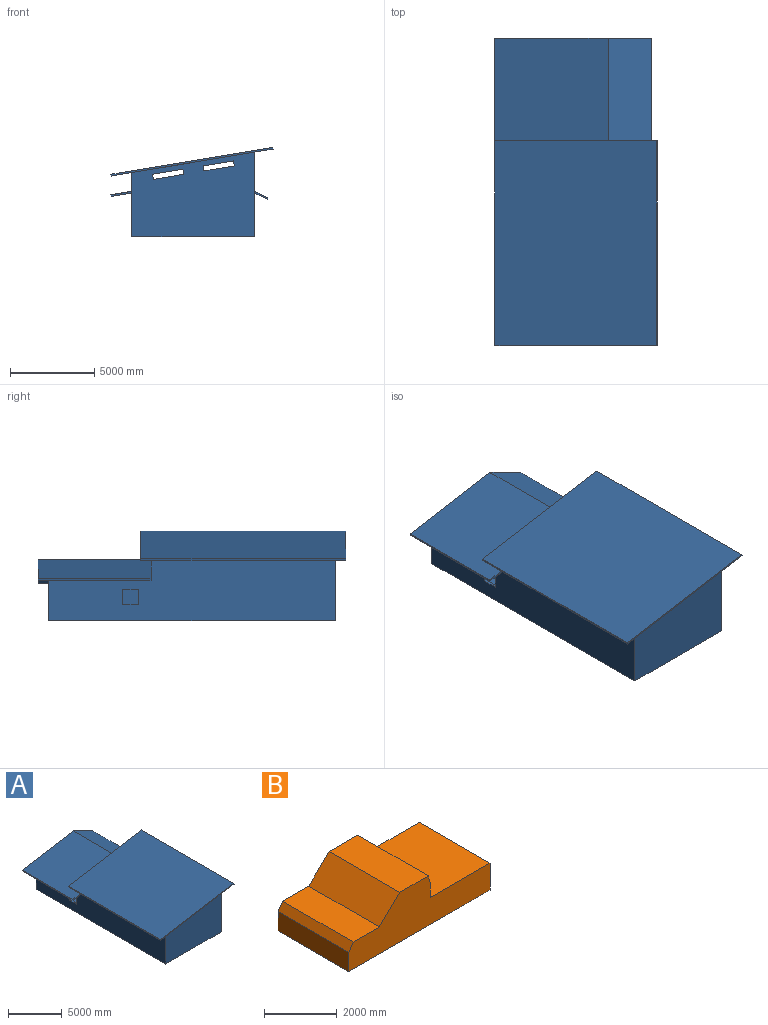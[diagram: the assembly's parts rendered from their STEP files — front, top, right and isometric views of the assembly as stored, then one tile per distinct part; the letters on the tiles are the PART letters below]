
ASSEMBLY  parts=2 mates=1
PART A: 106 faces, bbox 9637.6x18288x5310.4 mm
  f0: plane 7162.8x6096mm, normal (0,0,1), area 41367720.6mm2, adj f1,f2,f3,f6,f13,f15,f16,f41
  f1: plane 5181.6x3172.9mm, normal (0,1,0), area 13971038.2mm2, adj f0,f2,f3,f5,f88,f90,f91
  f2: plane 5943.6x2309.3mm, normal (1,0,0), area 12657180.9mm2, adj f0,f1,f5,f41,f56,f57,f58,f59
  f3: plane 5943.6x3172.9mm, normal (-1,0,0), area 15328305.8mm2, adj f0,f1,f5,f41,f49,f50,f51,f52
  f4: plane 10668x7162.8mm, normal (0,0,1), area 75715977.6mm2, adj f9,f10,f12,f13,f14,f44,f45,f47
  f5: plane 5943.6x5181.6mm, normal (0.16,0,-0.99), area 31222169mm2, adj f1,f2,f3,f41
  f6: plane 6096x3352.8mm, normal (1,0,0), area 16908539.1mm2, adj f0,f15,f16,f29,f49,f50,f51,f52
  f7: plane 7315.2x2335.5mm, normal (0,1,0), area 8165969.2mm2, adj f11,f13,f19,f26,f27,f60,f61,f62
  f8: plane 7315.2x5029.2mm, normal (0,-1,0), area 31215421.4mm2, adj f11,f13,f17,f19,f68,f69,f70,f71
  f9: plane 7010.4x4799.8mm, normal (0,1,0), area 28438179.7mm2, adj f4,f12,f14,f42,f68,f69,f70,f71
  f10: plane 7010.4x4799.8mm, normal (0,-1,0), area 28438179.7mm2, adj f4,f12,f14,f42,f60,f61,f62,f63
  f11: plane 17068.8x3810mm, normal (-1,0,0), area 56763757.4mm2, adj f7,f8,f15,f17,f19,f24,f32,f56
  f12: plane 10668x3631.4mm, normal (1,0,0), area 38739735.5mm2, adj f4,f9,f10,f42
  f13: plane 17068.8x5029.2mm, normal (1,0,0), area 33816706.6mm2, adj f0,f4,f7,f8,f15,f16,f17,f19
  f14: plane 10668x4799.8mm, normal (-1,0,0), area 28907497.1mm2, adj f4,f9,f10,f42,f43,f44,f45,f46
  f15: plane 7315.2x3505.2mm, normal (0,1,0), area 15329001.6mm2, adj f0,f6,f11,f13,f17,f24,f33,f34
  f16: plane 3352.8x1828.8mm, normal (0,1,0), area 5295473.3mm2, adj f0,f6,f13,f29
  f17: plane 17068.8x7315.2mm, normal (0,0,-1), area 124861685.8mm2, adj f8,f11,f13,f15
  f18: plane 12192x100.12mm, normal (-0.99,0,-0.16), area 1237468.5mm2, adj f19,f21,f22,f23
  f19: plane 12192x9620.89mm, normal (0.16,0,-0.99), area 37540464.4mm2, adj f7,f8,f11,f13,f18,f20,f21,f22
  f20: plane 12192x100.12mm, normal (0.99,0,0.16), area 1237468.5mm2, adj f19,f21,f22,f23
  f21: plane 9637.58x1703.6mm, normal (0,-1,0), area 989974.8mm2, adj f18,f19,f20,f23
  f22: plane 9637.58x1703.6mm, normal (0,1,0), area 989974.8mm2, adj f18,f19,f20,f23
  f23: plane 12192x9620.89mm, normal (-0.16,0,0.99), area 118915891.2mm2, adj f18,f20,f21,f22
  f24: plane 6705.6x6705.6mm, normal (0.16,0,-0.99), area 11678880.7mm2, adj f11,f15,f28,f29,f31,f32
  f25: plane 762x483.9mm, normal (0,-1,0), area 78408.6mm2, adj f13,f26,f29,f30
  f26: plane 6705.6x2590.8mm, normal (0.45,0,0.89), area 19423457.4mm2, adj f7,f25,f27,f30,f31
  f27: plane 6722.29x6705.6mm, normal (-0.16,0,0.99), area 45698743.2mm2, adj f7,f26,f28,f31,f32
  f28: plane 6705.6x100.12mm, normal (-0.99,0,-0.16), area 680607.7mm2, adj f24,f27,f31,f32
  f29: plane 6705.6x2590.8mm, normal (-0.45,0,-0.89), area 19423457.4mm2, adj f6,f16,f24,f25,f30,f31
  f30: plane 6705.6x102.9mm, normal (1,0,0), area 689995.8mm2, adj f25,f26,f29,f31
  f31: plane 9313.09x1398.3mm, normal (0,1,0), area 957443.6mm2, adj f24,f26,f27,f28,f29,f30
  f32: plane 1235.89x306.1mm, normal (0,-1,0), area 126312.3mm2, adj f11,f24,f27,f28
  f33: plane 914.4x152.4mm, normal (0,0,-1), area 139354.6mm2, adj f15,f34,f36,f41
  f34: plane 914.4x152.4mm, normal (1,0,0), area 139354.6mm2, adj f15,f33,f35,f41
  f35: plane 914.4x152.4mm, normal (0,0,1), area 139354.6mm2, adj f15,f34,f36,f41
  f36: plane 914.4x152.4mm, normal (-1,0,0), area 139354.6mm2, adj f15,f33,f35,f41
  f37: plane 914.4x152.4mm, normal (-1,0,0), area 139354.6mm2, adj f15,f38,f40,f41
  f38: plane 914.4x152.4mm, normal (0,0,-1), area 139354.6mm2, adj f15,f37,f39,f41
  f39: plane 914.4x152.4mm, normal (1,0,0), area 139354.6mm2, adj f15,f38,f40,f41
  f40: plane 914.4x152.4mm, normal (0,0,1), area 139354.6mm2, adj f15,f37,f39,f41
  f41: plane 5181.6x3172.9mm, normal (0,-1,0), area 12298783.4mm2, adj f0,f2,f3,f5,f33,f34,f35,f36
  f42: plane 10668x7010.4mm, normal (0.16,0,-0.99), area 75818540mm2, adj f9,f10,f12,f14
  f43: plane 3657.6x152.4mm, normal (0,0,-1), area 557418.2mm2, adj f13,f14,f44,f45
  f44: plane 3657.6x152.4mm, normal (0,1,0), area 557418.2mm2, adj f4,f13,f14,f43
  f45: plane 3657.6x152.4mm, normal (0,-1,0), area 557418.2mm2, adj f4,f13,f14,f43
  f46: plane 3657.6x152.4mm, normal (0,0,-1), area 557418.2mm2, adj f13,f14,f47,f48
  f47: plane 2438.4x152.4mm, normal (0,1,0), area 371612.2mm2, adj f4,f13,f14,f46
  f48: plane 2438.4x152.4mm, normal (0,-1,0), area 371612.2mm2, adj f4,f13,f14,f46
  f49: plane 2031.8x152.4mm, normal (0,1,0), area 309645.8mm2, adj f0,f3,f6,f51
  f50: plane 2031.8x152.4mm, normal (0,-1,0), area 309645.8mm2, adj f0,f3,f6,f51
  f51: plane 914.4x152.4mm, normal (0,0,-1), area 139354.6mm2, adj f3,f6,f49,f50
  f52: plane 914.4x152.4mm, normal (0,-1,0), area 139354.6mm2, adj f3,f6,f53,f55
  f53: plane 914.4x152.4mm, normal (0,0,1), area 139354.6mm2, adj f3,f6,f52,f54
  f54: plane 914.4x152.4mm, normal (0,1,0), area 139354.6mm2, adj f3,f6,f53,f55
  f55: plane 914.4x152.4mm, normal (0,0,-1), area 139354.6mm2, adj f3,f6,f52,f54
  f56: plane 914.4x152.4mm, normal (0,0,-1), area 139354.6mm2, adj f2,f11,f57,f59
  f57: plane 914.4x152.4mm, normal (0,1,0), area 139354.6mm2, adj f2,f11,f56,f58
  f58: plane 914.4x152.4mm, normal (0,0,1), area 139354.6mm2, adj f2,f11,f57,f59
  f59: plane 914.4x152.4mm, normal (0,-1,0), area 139354.6mm2, adj f2,f11,f56,f58
  f60: plane 300.65x152.4mm, normal (-0.99,0,-0.16), area 46451.5mm2, adj f7,f10,f61,f63
  f61: plane 1803.92x300.65mm, normal (-0.16,0,0.99), area 278709.1mm2, adj f7,f10,f60,f62
  f62: plane 300.65x152.4mm, normal (0.99,0,0.16), area 46451.5mm2, adj f7,f10,f61,f63
  f63: plane 1803.92x300.65mm, normal (0.16,0,-0.99), area 278709.1mm2, adj f7,f10,f60,f62
  f64: plane 1803.92x300.65mm, normal (-0.16,0,0.99), area 278709.1mm2, adj f7,f10,f65,f67
  f65: plane 300.65x152.4mm, normal (0.99,0,0.16), area 46451.5mm2, adj f7,f10,f64,f66
  f66: plane 1803.92x300.65mm, normal (0.16,0,-0.99), area 278709.1mm2, adj f7,f10,f65,f67
  f67: plane 300.65x152.4mm, normal (-0.99,0,-0.16), area 46451.5mm2, adj f7,f10,f64,f66
  f68: plane 1803.92x300.65mm, normal (0.16,0,-0.99), area 278709.1mm2, adj f8,f9,f69,f71
  f69: plane 300.65x152.4mm, normal (0.99,0,0.16), area 46451.5mm2, adj f8,f9,f68,f70
  f70: plane 1803.92x300.65mm, normal (-0.16,0,0.99), area 278709.1mm2, adj f8,f9,f69,f71
  f71: plane 300.65x152.4mm, normal (-0.99,0,-0.16), area 46451.5mm2, adj f8,f9,f68,f70
  f72: plane 300.65x152.4mm, normal (-0.99,0,-0.16), area 46451.5mm2, adj f8,f9,f73,f75
  f73: plane 1803.92x300.65mm, normal (0.16,0,-0.99), area 278709.1mm2, adj f8,f9,f72,f74
  f74: plane 300.65x152.4mm, normal (0.99,0,0.16), area 46451.5mm2, adj f8,f9,f73,f75
  f75: plane 1803.92x300.65mm, normal (-0.16,0,0.99), area 278709.1mm2, adj f8,f9,f72,f74
  f76: plane 914.4x152.4mm, normal (0,-1,0), area 139354.6mm2, adj f3,f6,f77,f79
  f77: plane 914.4x152.4mm, normal (0,0,-1), area 139354.6mm2, adj f3,f6,f76,f78
  f78: plane 914.4x152.4mm, normal (0,1,0), area 139354.6mm2, adj f3,f6,f77,f79
  f79: plane 914.4x152.4mm, normal (0,0,1), area 139354.6mm2, adj f3,f6,f76,f78
  f80: plane 2286x787.41mm, normal (-1,0,0), area 1800008mm2, adj f0,f81,f86,f87
  f81: plane 2743.2x2286mm, normal (0,1,0), area 6270955.2mm2, adj f0,f2,f80,f87
  f82: plane 2743.2x2286mm, normal (0,-1,0), area 6270955.2mm2, adj f0,f2,f83,f87
  f83: plane 2286x152.4mm, normal (-1,0,0), area 348386.4mm2, adj f0,f82,f84,f87
  f84: plane 2286x101.59mm, normal (0,-1,0), area 232234.4mm2, adj f0,f83,f85,f87
  f85: plane 2286x1041.4mm, normal (1,0,0), area 2380628.8mm2, adj f0,f84,f86,f87
  f86: plane 2286x101.59mm, normal (0,1,0), area 232234.4mm2, adj f0,f80,f85,f87
  f87: plane 2844.79x1041.4mm, normal (0,0,1), area 384476.4mm2, adj f2,f80,f81,f82,f83,f84,f85,f86
  f88: plane 3200.4x2286mm, normal (1,0,0), area 7316114.4mm2, adj f0,f1,f89,f91
  f89: plane 2286x101.59mm, normal (0,1,0), area 232234.4mm2, adj f0,f88,f90,f91
  f90: plane 3200.4x2286mm, normal (-1,0,0), area 7316114.4mm2, adj f0,f1,f89,f91
  f91: plane 3200.4x101.59mm, normal (0,0,1), area 325128.1mm2, adj f1,f88,f89,f90
  f92: plane 2286x76.31mm, normal (-1,0,0), area 174437.1mm2, adj f0,f41,f93,f95
  f93: plane 2286x101.59mm, normal (0,-1,0), area 232234.4mm2, adj f0,f92,f94,f95
  f94: plane 2286x76.31mm, normal (1,0,0), area 174437.1mm2, adj f0,f41,f93,f95
  f95: plane 101.59x76.31mm, normal (0,0,1), area 7752mm2, adj f41,f92,f93,f94
  f96: plane 3352.8x304.8mm, normal (0,1,0), area 1021933.4mm2, adj f4,f97,f99,f100
  f97: plane 3352.8x304.8mm, normal (-1,0,0), area 1021933.4mm2, adj f4,f96,f98,f100
  f98: plane 3352.8x304.8mm, normal (0,-1,0), area 1021933.4mm2, adj f4,f97,f99,f100
  f99: plane 3352.8x304.8mm, normal (1,0,0), area 1021933.4mm2, adj f4,f96,f98,f100
  f100: plane 304.8x304.8mm, normal (0,0,1), area 92903mm2, adj f96,f97,f98,f99
  f101: plane 3352.8x304.8mm, normal (0,1,0), area 1021933.4mm2, adj f4,f102,f104,f105
  f102: plane 3352.8x304.8mm, normal (-1,0,0), area 1021933.4mm2, adj f4,f101,f103,f105
  f103: plane 3352.8x304.8mm, normal (0,-1,0), area 1021933.4mm2, adj f4,f102,f104,f105
  f104: plane 3352.8x304.8mm, normal (1,0,0), area 1021933.4mm2, adj f4,f101,f103,f105
  f105: plane 304.8x304.8mm, normal (0,0,1), area 92903mm2, adj f101,f102,f103,f104
PART B: 12 faces, bbox 5486.4x2743.2x1676.4 mm
  f0: plane 2743.2x1111.77mm, normal (0,0,1), area 3049806.9mm2, adj f1,f2,f7,f11
  f1: plane 5486.4x1676.4mm, normal (0,1,0), area 6158699mm2, adj f0,f3,f4,f5,f6,f7,f8,f9
  f2: plane 5486.4x1676.4mm, normal (0,-1,0), area 6158699mm2, adj f0,f3,f4,f5,f6,f7,f8,f9
  f3: plane 2743.2x648.4mm, normal (-1,0,0), area 1778690.2mm2, adj f1,f2,f5,f9
  f4: plane 2743.2x906.79mm, normal (1,0,0), area 2487509.6mm2, adj f1,f2,f5,f8
  f5: plane 5486.4x2743.2mm, normal (0,0,-1), area 15050292.5mm2, adj f1,f2,f3,f4
  f6: plane 2743.2x469.03mm, normal (1,0,0), area 1286651.1mm2, adj f1,f2,f7,f8
  f7: plane 2743.2x300.58mm, normal (0.97,0,0.25), area 851742.4mm2, adj f0,f1,f2,f6
  f8: plane 2743.2x2316.25mm, normal (0,0,1), area 6353927.5mm2, adj f1,f2,f4,f6
  f9: plane 2743.2x258.39mm, normal (-0.82,0,0.57), area 864500.5mm2, adj f1,f2,f3,f10
  f10: plane 2743.2x1012.32mm, normal (0,0,1), area 2777002.4mm2, adj f1,f2,f9,f11
  f11: plane 2743.2x787.8mm, normal (-0.7,0,0.72), area 3021176.1mm2, adj f0,f1,f2,f10
PLACE A t=(2032.5,3089.58,-206.37)mm fixed
PLACE B t=(-4315.38,-6504.89,-53.97)mm
MATE fastened B.f5 <-> A.f4  axis (0,0,1) through (-1572.18,-5133.29,-53.97)mm
